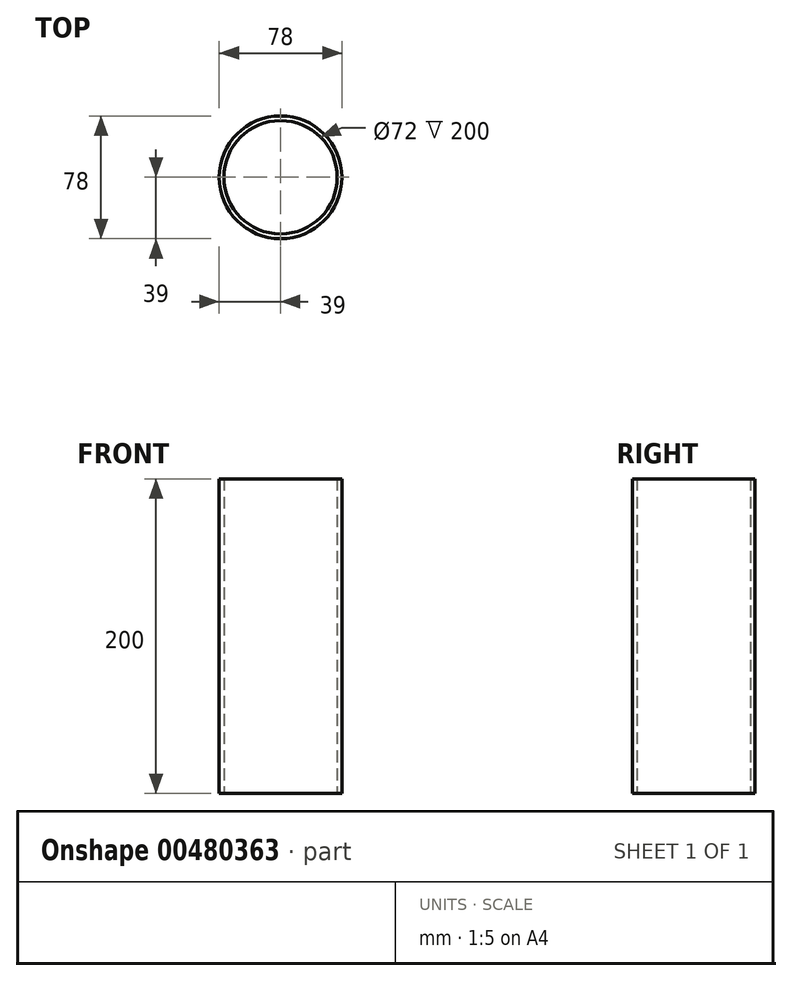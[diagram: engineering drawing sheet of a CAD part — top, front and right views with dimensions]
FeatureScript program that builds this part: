
annotation { "Feature Type Name" : "Feature", "Feature Type Description" : "" }
export const myFeature = defineFeature(function(context is Context, id is Id, definition is map)
    precondition{}
    {
        {
            var Q0;
            Q0=qCreatedBy(makeId("Top.planeOp"),FACE);
            var sketch = newSketch(context, id + "F0", { "sketchPlane" : qUnion([Q0])});
            skCircle(sketch, "E0", {"center": v(0, 0) * mm, "radius": 36 * mm});
            skCircle(sketch, "E1.0", {"center": v(0, 0) * mm, "radius": 39 * mm});
            skSolve(sketch);
        }
        {
            var Q0;
            Q0=makeQuery(id+"F0.imprint","IMPRINT",FACE,{"disambiguationData":[TD([[makeQuery(id+"F0.imprint","IMPRINT",EDGE,{"derivedFrom":sQuery(id+"F0.wireOp",EDGE,"E0")}),-1.0]])]});
            extrude(context, id + "F1", {"entities" : qUnion([Q0]), "depth" : 200 * mm, "offsetDistance" : 25 * mm});
        }
    });
